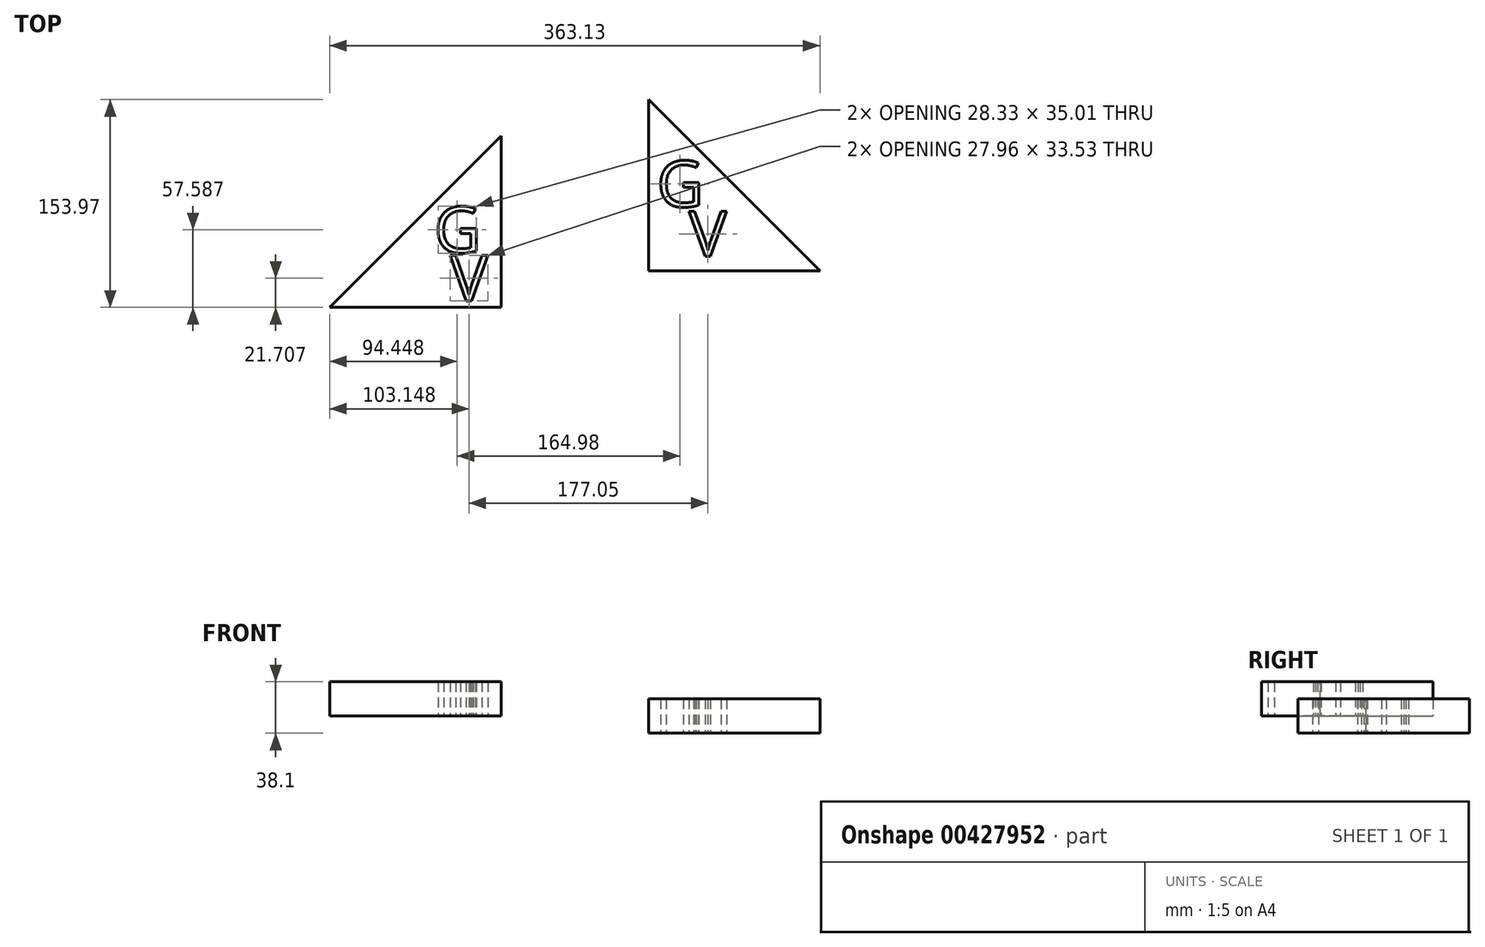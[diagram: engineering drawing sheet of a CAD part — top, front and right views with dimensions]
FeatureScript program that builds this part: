
annotation { "Feature Type Name" : "Feature", "Feature Type Description" : "" }
export const myFeature = defineFeature(function(context is Context, id is Id, definition is map)
    precondition{}
    {
        {
            var Q0;
            Q0=qCreatedBy(makeId("Top.planeOp"),FACE);
            var sketch = newSketch(context, id + "F0", { "sketchPlane" : qUnion([Q0])});
            skLineSegment(sketch, "E0", {"start": v(0, 0) * mm, "end": v(0, 127) * mm});
            skLineSegment(sketch, "E1", {"start": v(0, 0) * mm, "end": v(127, 0) * mm});
            skLineSegment(sketch, "E2", {"start": v(0, 127) * mm, "end": v(127, 0) * mm});
            skText(sketch, "E3", { "text": "G", "fontName": "OpenSans-Regular.ttf"});
            skText(sketch, "E4", { "text": "V", "fontName": "OpenSans-Regular.ttf"});
            const initialGuessF0  = {"E3": [0.00622, 0.04759, 1, 0, 0.03435], "E4": [0.03009, 0.01083, 1, 0, 0.03382]};
            skSetInitialGuess(sketch, initialGuessF0);
            skSolve(sketch);
        }
        {
            var Q0;
            Q0=qSketchRegion(id+"F0",true);
            extrude(context, id + "F1", {"entities" : qUnion([Q0]), "depth" : 25.4 * mm, "symmetric" : true});
        }
        {
            var Q0;
            Q0=qCreatedBy(makeId("Top.planeOp"),FACE);
            var sketch = newSketch(context, id + "F2", { "sketchPlane" : qUnion([Q0])});
            skLineSegment(sketch, "E5", {"start": v(0, 0) * mm, "end": v(0, 127) * mm});
            skLineSegment(sketch, "E6", {"start": v(-109.13, -26.97) * mm, "end": v(-109.13, 100.03) * mm});
            skLineSegment(sketch, "E7", {"start": v(-109.13, -26.97) * mm, "end": v(-236.13, -26.97) * mm});
            skLineSegment(sketch, "E8", {"start": v(-236.13, -26.97) * mm, "end": v(-109.13, 100.03) * mm});
            skText(sketch, "E9", { "text": "G", "fontName": "OpenSans-Regular.ttf"});
            skText(sketch, "E10", { "text": "V", "fontName": "OpenSans-Regular.ttf"});
            const initialGuessF2  = {"E9": [-0.15876, 0.01358, 1, 0, 0.03435], "E10": [-0.14696, -0.02203, 1, 0, 0.03382]};
            skSetInitialGuess(sketch, initialGuessF2);
            skSolve(sketch);
        }
        {
            var Q0;
            Q0=qSketchRegion(id+"F2",true);
            extrude(context, id + "F3", {"entities" : qUnion([Q0]), "depth" : 25.4 * mm});
        }
    });
